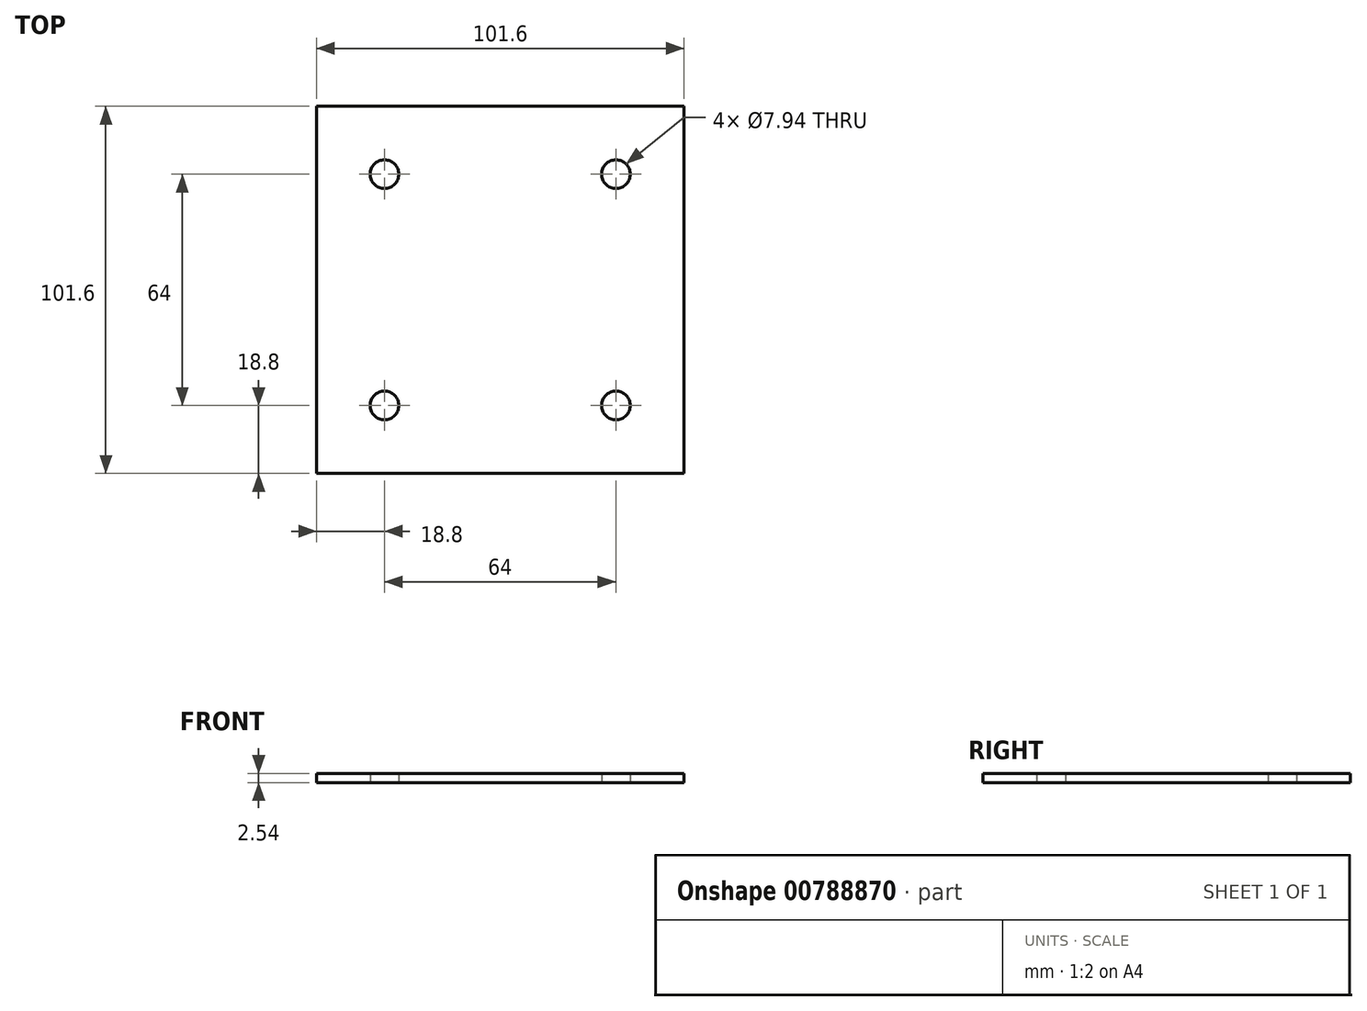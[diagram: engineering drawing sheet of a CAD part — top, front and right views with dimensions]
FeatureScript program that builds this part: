
annotation { "Feature Type Name" : "Feature", "Feature Type Description" : "" }
export const myFeature = defineFeature(function(context is Context, id is Id, definition is map)
    precondition{}
    {
        {
            var Q0;
            Q0=qCreatedBy(makeId("Top.planeOp"),FACE);
            var sketch = newSketch(context, id + "F0", { "sketchPlane" : qUnion([Q0])});
            skCircle(sketch, "E0", {"center": v(0, 0) * mm, "radius": 3.97 * mm});
            skCircle(sketch, "E1", {"center": v(-64, 0) * mm, "radius": 3.97 * mm});
            skCircle(sketch, "E2", {"center": v(-64, -64) * mm, "radius": 3.97 * mm});
            skCircle(sketch, "E3", {"center": v(0, -64) * mm, "radius": 3.97 * mm});
            skLineSegment(sketch, "E4.bottom", {"start": v(-82.8, 18.8) * mm, "end": v(18.8, 18.8) * mm});
            skLineSegment(sketch, "E4.top", {"start": v(-82.8, -82.8) * mm, "end": v(18.8, -82.8) * mm});
            skLineSegment(sketch, "E4.left", {"start": v(-82.8, 18.8) * mm, "end": v(-82.8, -82.8) * mm});
            skLineSegment(sketch, "E4.right", {"start": v(18.8, 18.8) * mm, "end": v(18.8, -82.8) * mm});
            skLineSegment(sketch, "E5", {"start": v(-64, 0) * mm, "end": v(0, 0) * mm, "construction": true});
            skPoint(sketch, "E6", {"position": v(-32, 0) * mm});
            skPoint(sketch, "E7", {"position": v(-32, 18.8) * mm});
            skLineSegment(sketch, "E8", {"start": v(0, 0) * mm, "end": v(0, -64) * mm, "construction": true});
            skPoint(sketch, "E9", {"position": v(0, -32) * mm});
            skPoint(sketch, "E10", {"position": v(18.8, -32) * mm});
            skSolve(sketch);
        }
        {
            var Q0;
            Q0=makeQuery(id+"F0.imprint","IMPRINT",FACE,{"disambiguationData":[TD([[makeQuery(id+"F0.imprint","IMPRINT",EDGE,{"derivedFrom":sQuery(id+"F0.wireOp",EDGE,"E0")}),-1.0]])]});
            extrude(context, id + "F1", {"entities" : qUnion([Q0]), "depth" : 2.54 * mm, "offsetDistance" : 25.4 * mm});
        }
    });
